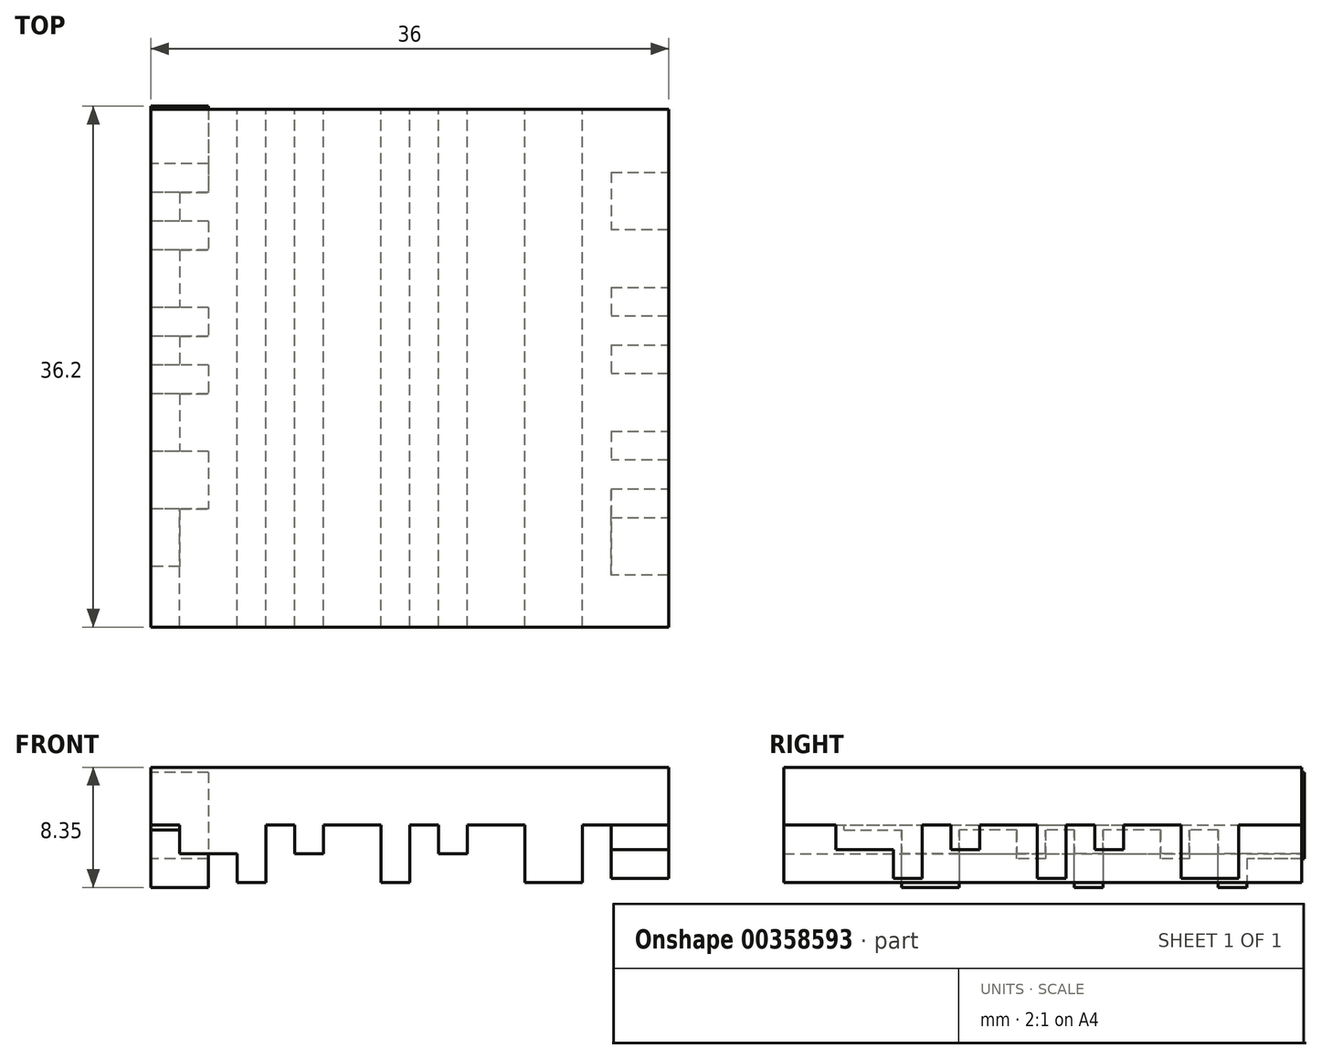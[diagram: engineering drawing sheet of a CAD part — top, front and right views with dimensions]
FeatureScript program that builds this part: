
annotation { "Feature Type Name" : "Feature", "Feature Type Description" : "" }
export const myFeature = defineFeature(function(context is Context, id is Id, definition is map)
    precondition{}
    {
        {
            var Q0;
            Q0=qCreatedBy(makeId("Front.planeOp"),FACE);
            var sketch = newSketch(context, id + "F0", { "sketchPlane" : qUnion([Q0])});
            skLineSegment(sketch, "E0.bottom", {"start": v(18, -2) * mm, "end": v(-18, -2) * mm});
            skLineSegment(sketch, "E0.top", {"start": v(18, 2) * mm, "end": v(-18, 2) * mm});
            skLineSegment(sketch, "E0.left", {"start": v(18, -2) * mm, "end": v(18, 2) * mm});
            skLineSegment(sketch, "E0.right", {"start": v(-18, -2) * mm, "end": v(-18, 2) * mm});
            skPoint(sketch, "E0.middle", {"position": v(0, 0) * mm});
            skLineSegment(sketch, "E1", {"start": v(-18, -2) * mm, "end": v(-16, -2) * mm});
            skLineSegment(sketch, "E2", {"start": v(-16, -2) * mm, "end": v(-16, -4) * mm});
            skLineSegment(sketch, "E3", {"start": v(-16, -4) * mm, "end": v(-12, -4) * mm});
            skLineSegment(sketch, "E4", {"start": v(-12, -4) * mm, "end": v(-12, -6) * mm});
            skLineSegment(sketch, "E5", {"start": v(-12, -6) * mm, "end": v(-10, -6) * mm});
            skLineSegment(sketch, "E6", {"start": v(-10, -6) * mm, "end": v(-10, -2) * mm});
            skLineSegment(sketch, "E7", {"start": v(-10, -2) * mm, "end": v(-8, -2) * mm});
            skLineSegment(sketch, "E8", {"start": v(-8, -2) * mm, "end": v(-8, -4) * mm});
            skLineSegment(sketch, "E9", {"start": v(-8, -4) * mm, "end": v(-6, -4) * mm});
            skLineSegment(sketch, "E10", {"start": v(-6, -4) * mm, "end": v(-6, -2) * mm});
            skLineSegment(sketch, "E11", {"start": v(-6, -2) * mm, "end": v(-2, -2) * mm});
            skLineSegment(sketch, "E12", {"start": v(-2, -2) * mm, "end": v(-2, -6) * mm});
            skLineSegment(sketch, "E13", {"start": v(-2, -6) * mm, "end": v(0, -6) * mm});
            skLineSegment(sketch, "E14", {"start": v(0, -6) * mm, "end": v(0, -2) * mm});
            skLineSegment(sketch, "E15", {"start": v(0, -2) * mm, "end": v(2, -2) * mm});
            skLineSegment(sketch, "E16", {"start": v(2, -2) * mm, "end": v(2, -4) * mm});
            skLineSegment(sketch, "E17", {"start": v(2, -4) * mm, "end": v(4, -4) * mm});
            skLineSegment(sketch, "E18", {"start": v(4, -4) * mm, "end": v(4, -2) * mm});
            skLineSegment(sketch, "E19", {"start": v(4, -2) * mm, "end": v(8, -2) * mm});
            skLineSegment(sketch, "E20", {"start": v(8, -2) * mm, "end": v(8, -6) * mm});
            skLineSegment(sketch, "E21", {"start": v(8, -6) * mm, "end": v(12, -6) * mm});
            skLineSegment(sketch, "E22", {"start": v(12, -6) * mm, "end": v(12, -2) * mm});
            skLineSegment(sketch, "E23", {"start": v(12, -2) * mm, "end": v(16, -2) * mm});
            skSolve(sketch);
        }
        {
            var Q0;
            Q0 = qSketchRegion(id + "F0", true);
            extrude(context, id + "F1", {"entities" : qUnion([Q0]), "depth" : 36 * mm});
        }
        {
            var Q0;
            Q0=makeQuery(id+"F1.opExtrude","SWEPT_FACE",FACE,{"disambiguationData":[OSD([sQuery(id+"F0.wireOp",EDGE,"E0.left")])]});
            var sketch = newSketch(context, id + "F2", { "sketchPlane" : qUnion([Q0])});
            skLineSegment(sketch, "E24.bottom", {"start": v(-0.38, -1.72) * mm, "end": v(-32.38, -1.72) * mm});
            skLineSegment(sketch, "E24.top", {"start": v(1.62, 2.28) * mm, "end": v(-34.38, 2.28) * mm});
            skPoint(sketch, "E24.middle", {"position": v(-16.38, 0.28) * mm});
            skLineSegment(sketch, "E25", {"start": v(-32.38, -1.72) * mm, "end": v(-32.38, -3.72) * mm});
            skLineSegment(sketch, "E26", {"start": v(-32.38, -3.72) * mm, "end": v(-28.38, -3.72) * mm});
            skLineSegment(sketch, "E27", {"start": v(-28.38, -3.72) * mm, "end": v(-28.38, -5.72) * mm});
            skLineSegment(sketch, "E28", {"start": v(-28.38, -5.72) * mm, "end": v(-26.38, -5.72) * mm});
            skLineSegment(sketch, "E29", {"start": v(-26.38, -5.72) * mm, "end": v(-26.38, -1.72) * mm});
            skLineSegment(sketch, "E30", {"start": v(-26.38, -1.72) * mm, "end": v(-24.38, -1.72) * mm});
            skLineSegment(sketch, "E31", {"start": v(-24.38, -1.72) * mm, "end": v(-24.38, -3.72) * mm});
            skLineSegment(sketch, "E32", {"start": v(-24.38, -3.72) * mm, "end": v(-22.38, -3.72) * mm});
            skLineSegment(sketch, "E33", {"start": v(-22.38, -3.72) * mm, "end": v(-22.38, -1.72) * mm});
            skLineSegment(sketch, "E34", {"start": v(-22.38, -1.72) * mm, "end": v(-18.38, -1.72) * mm});
            skLineSegment(sketch, "E35", {"start": v(-18.38, -1.72) * mm, "end": v(-18.38, -5.72) * mm});
            skLineSegment(sketch, "E36", {"start": v(-18.38, -5.72) * mm, "end": v(-16.38, -5.72) * mm});
            skLineSegment(sketch, "E37", {"start": v(-16.38, -5.72) * mm, "end": v(-16.38, -1.72) * mm});
            skLineSegment(sketch, "E38", {"start": v(-16.38, -1.72) * mm, "end": v(-14.38, -1.72) * mm});
            skLineSegment(sketch, "E39", {"start": v(-14.38, -1.72) * mm, "end": v(-14.38, -3.72) * mm});
            skLineSegment(sketch, "E40", {"start": v(-14.38, -3.72) * mm, "end": v(-12.38, -3.72) * mm});
            skLineSegment(sketch, "E41", {"start": v(-12.38, -3.72) * mm, "end": v(-12.38, -1.72) * mm});
            skLineSegment(sketch, "E42", {"start": v(-12.38, -1.72) * mm, "end": v(-8.38, -1.72) * mm});
            skLineSegment(sketch, "E43", {"start": v(-8.38, -1.72) * mm, "end": v(-8.38, -5.72) * mm});
            skLineSegment(sketch, "E44", {"start": v(-8.38, -5.72) * mm, "end": v(-4.38, -5.72) * mm});
            skLineSegment(sketch, "E45", {"start": v(-4.38, -5.72) * mm, "end": v(-4.38, -1.72) * mm});
            skLineSegment(sketch, "E46", {"start": v(-4.38, -1.72) * mm, "end": v(-0.38, -1.72) * mm});
            skPoint(sketch, "E47.orphan", {"position": v(1.62, -1.72) * mm});
            skLineSegment(sketch, "E48", {"start": v(0, -2) * mm, "end": v(0, 2) * mm});
            skPoint(sketch, "E49.orphan", {"position": v(-34.38, -1.72) * mm});
            skLineSegment(sketch, "E50", {"start": v(-36, -2) * mm, "end": v(-36, 2) * mm});
            skSolve(sketch);
        }
        {
            var Q0;
            Q0 = qSketchRegion(id + "F2", true);
            extrude(context, id + "F3", {"entities" : qUnion([Q0]), "operationType" : NewBodyOperationType.ADD, "oppositeDirection" : true, "depth" : 4 * mm});
        }
        {
            var Q0;
            Q0=makeQuery(id+"F1.opExtrude","SWEPT_FACE",FACE,{"disambiguationData":[OSD([sQuery(id+"F0.wireOp",EDGE,"E0.right")])]});
            var sketch = newSketch(context, id + "F4", { "sketchPlane" : qUnion([Q0])});
            skLineSegment(sketch, "E51.bottom", {"start": v(31.8, -2.35) * mm, "end": v(-0.2, -2.35) * mm});
            skLineSegment(sketch, "E51.top", {"start": v(31.8, 1.65) * mm, "end": v(-0.2, 1.65) * mm});
            skPoint(sketch, "E51.middle", {"position": v(15.8, -0.35) * mm});
            skLineSegment(sketch, "E52", {"start": v(-0.2, -2.35) * mm, "end": v(-0.2, -4.35) * mm});
            skLineSegment(sketch, "E53", {"start": v(-0.2, -4.35) * mm, "end": v(3.8, -4.35) * mm});
            skLineSegment(sketch, "E54", {"start": v(3.8, -4.35) * mm, "end": v(3.8, -6.35) * mm});
            skLineSegment(sketch, "E55", {"start": v(3.8, -6.35) * mm, "end": v(5.8, -6.35) * mm});
            skLineSegment(sketch, "E56", {"start": v(5.8, -6.35) * mm, "end": v(5.8, -2.35) * mm});
            skLineSegment(sketch, "E57", {"start": v(5.8, -2.35) * mm, "end": v(7.8, -2.35) * mm});
            skLineSegment(sketch, "E58", {"start": v(7.8, -2.35) * mm, "end": v(7.8, -4.35) * mm});
            skLineSegment(sketch, "E59", {"start": v(7.8, -4.35) * mm, "end": v(9.8, -4.35) * mm});
            skLineSegment(sketch, "E60", {"start": v(9.8, -4.35) * mm, "end": v(9.8, -2.35) * mm});
            skLineSegment(sketch, "E61", {"start": v(9.8, -2.35) * mm, "end": v(13.8, -2.35) * mm});
            skLineSegment(sketch, "E62", {"start": v(13.8, -2.35) * mm, "end": v(13.8, -6.35) * mm});
            skLineSegment(sketch, "E63", {"start": v(13.8, -6.35) * mm, "end": v(15.8, -6.35) * mm});
            skLineSegment(sketch, "E64", {"start": v(15.8, -6.35) * mm, "end": v(15.8, -2.35) * mm});
            skLineSegment(sketch, "E65", {"start": v(15.8, -2.35) * mm, "end": v(17.8, -2.35) * mm});
            skLineSegment(sketch, "E66", {"start": v(17.8, -2.35) * mm, "end": v(17.8, -4.35) * mm});
            skLineSegment(sketch, "E67", {"start": v(17.8, -4.35) * mm, "end": v(19.8, -4.35) * mm});
            skLineSegment(sketch, "E68", {"start": v(19.8, -4.35) * mm, "end": v(19.8, -2.35) * mm});
            skLineSegment(sketch, "E69", {"start": v(19.8, -2.35) * mm, "end": v(23.8, -2.35) * mm});
            skLineSegment(sketch, "E70", {"start": v(23.8, -2.35) * mm, "end": v(23.8, -6.35) * mm});
            skLineSegment(sketch, "E71", {"start": v(23.8, -6.35) * mm, "end": v(27.8, -6.35) * mm});
            skLineSegment(sketch, "E72", {"start": v(27.8, -6.35) * mm, "end": v(27.8, -2.35) * mm});
            skLineSegment(sketch, "E73", {"start": v(27.8, -2.35) * mm, "end": v(31.8, -2.35) * mm});
            skLineSegment(sketch, "E74", {"start": v(-0.2, -2.35) * mm, "end": v(-0.2, 1.65) * mm});
            skPoint(sketch, "E75.orphan", {"position": v(-2.2, -2.35) * mm});
            skPoint(sketch, "E76.orphan", {"position": v(-2.2, 1.65) * mm});
            skLineSegment(sketch, "E77", {"start": v(31.8, -2.35) * mm, "end": v(31.8, 1.65) * mm});
            skPoint(sketch, "E78.orphan", {"position": v(33.8, -2.35) * mm});
            skPoint(sketch, "E79.orphan", {"position": v(33.8, 1.65) * mm});
            skSolve(sketch);
        }
        {
            var Q0;
            Q0 = qSketchRegion(id + "F4", true);
            extrude(context, id + "F5", {"entities" : qUnion([Q0]), "operationType" : NewBodyOperationType.ADD, "oppositeDirection" : true, "depth" : 4 * mm});
        }
    });
